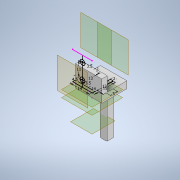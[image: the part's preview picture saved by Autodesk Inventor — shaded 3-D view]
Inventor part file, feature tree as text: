
AUTODESK INVENTOR PART (.ipt)
format: ipt  version: 2021 (Build 250183000, 183)  size: 188,928 bytes
history: native  units: mm
features: sketch x10, extrude x7, plane x6, projected_geometry x2
ambient origin geometry x8: Origin, YZ Plane, XZ Plane, XY Plane, X Axis, Y Axis, Z Axis, Center Point
bodies: Solid1 (feature_tree)
feature tree (25):
  sketch  "Sketch1"  dims[d0=13.0mm d1=2.0mm]
  plane  "Work Plane2"
  sketch  "Sketch2"  dims[d2=15.0mm d3=14.0mm]
  plane  "Work Plane5"
  extrude  "Extrusion3"  Depth=2.0mm
  plane  "Work Plane6"
  sketch  "Sketch4"  dims[d8=4.5mm d9=3.5mm]
  plane  "Work Plane1"
  extrude  "Extrusion4"  Depth=14.0mm
  plane  "Work Plane3"
  extrude  "Extrusion5"  Depth=13.0mm
  plane  "Work Plane4"
  extrude  "Extrusion7"  Depth=4.5mm
  extrude  "Extrusion9"  Depth=3.5mm
  extrude  "Extrusion10"  Depth=5.0mm
  extrude  "Extrusion11"  Depth=5.0mm TaperAngle=0.0deg
  sketch  "Sketch3"  dims[d4=2.0mm d5=13.0mm]
  sketch  "Sketch5"  dims[d10=11.0mm d11=3.5mm]
  sketch  "Sketch6"  dims[d14=5.0mm d15=0.0mm d16=14.0mm]
  sketch  "Sketch9"  dims[d17=5.0mm d20=20.0mm d21=0.0mm]
  projected_geometry  "Projected Loop1"
  sketch  "Sketch11"  dims[d25=2.5mm]
  projected_geometry  "Projected Loop2"
  sketch  "Sketch12"  dims[d26=5.0mm]
  sketch  "Sketch13"  dims[d27=5.0mm d28=20.0mm d29=0.0mm d31=12.5mm d35=15.0mm d36=0.0mm d39=5.0mm d40=5.0mm d41=5.0mm d42=0.0mm d43=4.0mm d44=0.0mm d45=0.0mm d46=10.0mm d47=0.0mm]
